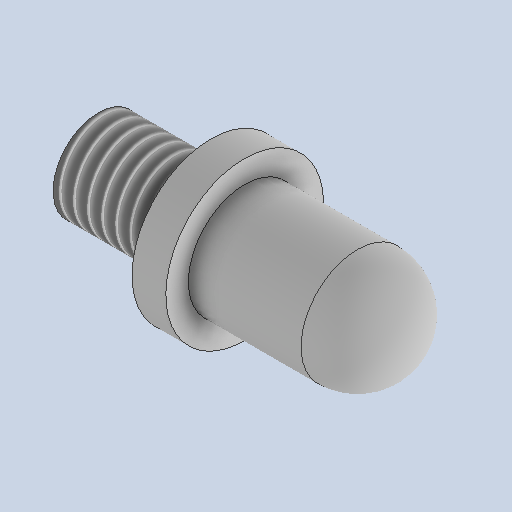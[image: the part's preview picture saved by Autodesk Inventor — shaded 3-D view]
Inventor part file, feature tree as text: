
AUTODESK INVENTOR PART (.ipt)
format: ipt  version: 2025.1 (Build 291241000, 241)  size: 161,280 bytes
history: native  units: mm
features: sketch x2, revolve x1, thread x1, hole x1
ambient origin geometry x8: Origin, YZ Plane, XZ Plane, XY Plane, X Axis, Y Axis, Z Axis, Center Point
bodies: Volumenkörper1 (feature_tree)
feature tree (5):
  revolve  "Umdrehung1"
  thread  "Gewinde1"  [1 undecoded]
  hole  "Bohrung1"  [1 undecoded]
  sketch  "Skizze1"  dims[d1=10.0mm d2=15.0mm]
  sketch  "Skizze2"  dims[d3=14.0mm d4=8.0mm d5=10.0mm d6=90.0deg d7=10.0mm d8=0.0mm d9=5.0mm d10=6.0mm d11=4.0mm d12=2.0mm d13=90.0deg d14=25.0mm d15=0.0mm]
note: 2 required parameter values undecoded (feature->parameter linkage not recoverable at this tier; creation-order binding heuristic only, values carry confidence <= 0.55)
